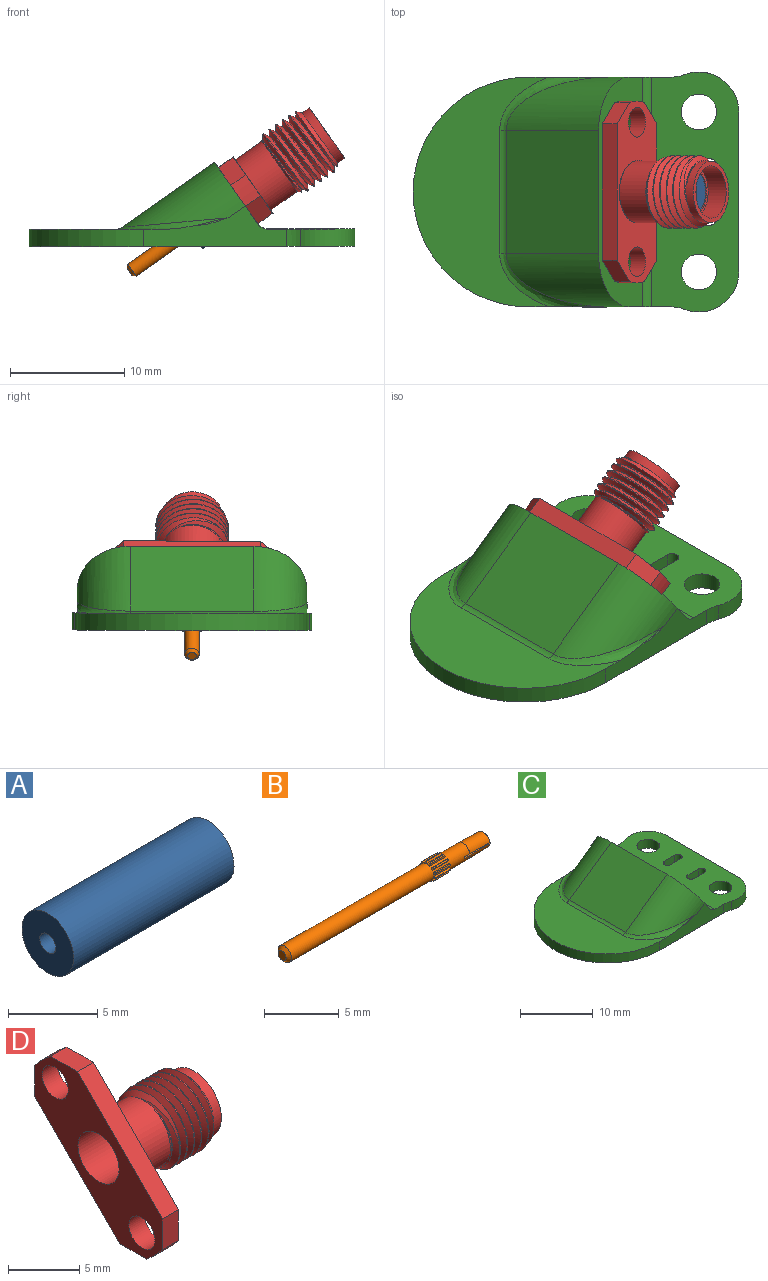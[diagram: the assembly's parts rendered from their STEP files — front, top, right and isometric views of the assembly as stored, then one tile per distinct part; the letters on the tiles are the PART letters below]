
ASSEMBLY  parts=4 mates=5
PART A: 4 faces, bbox 12.7x4.1x4.1 mm
  f0: plane 4.09x4.09mm, normal (-1,0,0), area 11.9mm2, adj f1,f3
  f1: cylinder r=0.64mm len=12.7mm, axis (-1,0,0), area 50.7mm2, adj f0,f2
  f2: plane 4.09x4.09mm, normal (1,0,0), area 11.9mm2, adj f1,f3
  f3: cylinder r=2.04mm len=12.7mm, axis (-1,0,0), area 163.2mm2, adj f0,f2
PART B: 81 faces, bbox 19.1x1.5x1.5 mm
  f0: cone r=0.76mm half-angle=60deg, axis (-1,0,0), area 0mm2, adj f1,f40,f76,f79
  f1: cylinder r=0.76mm len=1.38mm, axis (1,0,0), area 0.1mm2, adj f0,f2,f76,f79
  f2: cone r=0.64mm half-angle=60deg, axis (1,0,0), area 0mm2, adj f1,f40,f76,f79
  f3: cone r=0.76mm half-angle=60deg, axis (-1,0,0), area 0mm2, adj f4,f40,f74,f77
  f4: cylinder r=0.76mm len=1.38mm, axis (1,0,0), area 0.1mm2, adj f3,f5,f74,f77
  f5: cone r=0.64mm half-angle=60deg, axis (1,0,0), area 0mm2, adj f4,f40,f74,f77
  f6: cone r=0.76mm half-angle=60deg, axis (-1,0,0), area 0mm2, adj f7,f40,f72,f75
  f7: cylinder r=0.76mm len=1.38mm, axis (1,0,0), area 0.1mm2, adj f6,f8,f72,f75
  f8: cone r=0.64mm half-angle=60deg, axis (1,0,0), area 0mm2, adj f7,f40,f72,f75
  f9: cone r=0.76mm half-angle=60deg, axis (-1,0,0), area 0mm2, adj f10,f40,f70,f73
  f10: cylinder r=0.76mm len=1.38mm, axis (1,0,0), area 0.1mm2, adj f9,f11,f70,f73
  f11: cone r=0.64mm half-angle=60deg, axis (1,0,0), area 0mm2, adj f10,f40,f70,f73
  f12: cone r=0.76mm half-angle=60deg, axis (-1,0,0), area 0mm2, adj f13,f40,f68,f71
  f13: cylinder r=0.76mm len=1.38mm, axis (1,0,0), area 0.1mm2, adj f12,f14,f68,f71
  f14: cone r=0.64mm half-angle=60deg, axis (1,0,0), area 0mm2, adj f13,f40,f68,f71
  f15: cone r=0.76mm half-angle=60deg, axis (-1,0,0), area 0mm2, adj f16,f40,f66,f69
  f16: cylinder r=0.76mm len=1.38mm, axis (1,0,0), area 0.1mm2, adj f15,f17,f66,f69
  f17: cone r=0.64mm half-angle=60deg, axis (1,0,0), area 0mm2, adj f16,f40,f66,f69
  f18: cone r=0.76mm half-angle=60deg, axis (-1,0,0), area 0mm2, adj f19,f40,f64,f67
  f19: cylinder r=0.76mm len=1.38mm, axis (1,0,0), area 0.1mm2, adj f18,f20,f64,f67
  f20: cone r=0.64mm half-angle=60deg, axis (1,0,0), area 0mm2, adj f19,f40,f64,f67
  f21: cone r=0.76mm half-angle=60deg, axis (-1,0,0), area 0mm2, adj f22,f40,f63,f65
  f22: cylinder r=0.76mm len=1.38mm, axis (1,0,0), area 0.1mm2, adj f21,f23,f63,f65
  f23: cone r=0.64mm half-angle=60deg, axis (1,0,0), area 0mm2, adj f22,f40,f63,f65
  f24: cone r=0.76mm half-angle=60deg, axis (-1,0,0), area 0mm2, adj f25,f40,f60,f62
  f25: cylinder r=0.76mm len=1.38mm, axis (1,0,0), area 0.1mm2, adj f24,f26,f60,f62
  f26: cone r=0.64mm half-angle=60deg, axis (1,0,0), area 0mm2, adj f25,f40,f60,f62
  f27: cone r=0.76mm half-angle=60deg, axis (-1,0,0), area 0mm2, adj f28,f40,f58,f61
  f28: cylinder r=0.76mm len=1.38mm, axis (1,0,0), area 0.1mm2, adj f27,f29,f58,f61
  f29: cone r=0.64mm half-angle=60deg, axis (1,0,0), area 0mm2, adj f28,f40,f58,f61
  f30: cone r=0.76mm half-angle=60deg, axis (-1,0,0), area 0mm2, adj f31,f40,f56,f59
  f31: cylinder r=0.76mm len=1.38mm, axis (1,0,0), area 0.1mm2, adj f30,f32,f56,f59
  f32: cone r=0.64mm half-angle=60deg, axis (1,0,0), area 0mm2, adj f31,f40,f56,f59
  f33: plane 0.18x0.15mm, normal (1,0,0), area 0mm2, adj f36,f40,f42,f50
  f34: plane 0.18x0.15mm, normal (1,0,0), area 0mm2, adj f36,f40,f43,f49
  f35: cone r=0.46mm half-angle=59deg, axis (1,0,0), area 0.8mm2, adj f36
  f36: cylinder r=0.46mm len=1.02mm, axis (1,0,0), area 2.8mm2, adj f33,f34,f35,f42,f43,f47,f49,f50
  f37: cone r=0.76mm half-angle=60deg, axis (-1,0,0), area 0mm2, adj f38,f40,f57,f78
  f38: cylinder r=0.76mm len=1.38mm, axis (1,0,0), area 0.1mm2, adj f37,f39,f57,f78
  f39: cone r=0.64mm half-angle=60deg, axis (1,0,0), area 0mm2, adj f38,f40,f57,f78
  f40: cylinder r=0.64mm len=16.89mm, axis (1,0,0), area 64mm2, adj f0,f2,f3,f5,f6,f8,f9,f11
  f41: plane 0.76x0.76mm, normal (-1,0,0), area 0.5mm2, adj f80
  f42: plane 0.51x0.18mm, normal (0,0,-1), area 0.1mm2, adj f33,f36,f40,f46
  f43: plane 0.51x0.18mm, normal (0,0,-1), area 0.1mm2, adj f34,f36,f40,f48
  f44: plane 1.26x0.55mm, normal (1,0,0), area 0.3mm2, adj f45,f46,f47,f48
  f45: bspline ~1.91x1.26mm, area 3.5mm2, adj f40,f44,f46,f48
  f46: plane 1.91x0.18mm, normal (-0.03,0,-1), area 0.3mm2, adj f42,f44,f45,f47
  f47: bspline ~1.91x0.9mm, area 2.4mm2, adj f36,f44,f46,f48
  f48: plane 1.91x0.19mm, normal (-0.03,0,-1), area 0.3mm2, adj f43,f44,f45,f47
  f49: plane 0.51x0.18mm, normal (0,0,1), area 0.1mm2, adj f34,f36,f40,f52
  f50: plane 0.51x0.18mm, normal (0,0,1), area 0.1mm2, adj f33,f36,f40,f54
  f51: plane 1.26x0.55mm, normal (1,0,0), area 0.3mm2, adj f52,f53,f54,f55
  f52: plane 1.91x0.19mm, normal (-0.03,0,1), area 0.3mm2, adj f49,f51,f53,f55
  f53: bspline ~1.91x0.9mm, area 2.4mm2, adj f36,f51,f52,f54
  f54: plane 1.91x0.18mm, normal (-0.03,0,1), area 0.3mm2, adj f50,f51,f53,f55
  f55: bspline ~1.91x1.26mm, area 3.5mm2, adj f40,f51,f52,f54
  f56: plane 1.53x0.12mm, normal (0,-0.87,0.5), area 0.2mm2, adj f30,f31,f32,f40
  f57: plane 1.53x0.12mm, normal (0,0.87,0.5), area 0.2mm2, adj f37,f38,f39,f40
  f58: plane 1.53x0.12mm, normal (0,-0.5,0.87), area 0.2mm2, adj f27,f28,f29,f40
  f59: plane 1.53x0.14mm, normal (0,1,0), area 0.2mm2, adj f30,f31,f32,f40
  f60: plane 1.53x0.14mm, normal (0,0,1), area 0.2mm2, adj f24,f25,f26,f40
  f61: plane 1.53x0.12mm, normal (0,0.87,-0.5), area 0.2mm2, adj f27,f28,f29,f40
  f62: plane 1.53x0.12mm, normal (0,0.5,-0.87), area 0.2mm2, adj f24,f25,f26,f40
  f63: plane 1.53x0.12mm, normal (0,0.5,0.87), area 0.2mm2, adj f21,f22,f23,f40
  f64: plane 1.53x0.12mm, normal (0,0.87,0.5), area 0.2mm2, adj f18,f19,f20,f40
  f65: plane 1.53x0.14mm, normal (0,0,-1), area 0.2mm2, adj f21,f22,f23,f40
  f66: plane 1.53x0.14mm, normal (0,1,0), area 0.2mm2, adj f15,f16,f17,f40
  f67: plane 1.53x0.12mm, normal (0,-0.5,-0.87), area 0.2mm2, adj f18,f19,f20,f40
  f68: plane 1.53x0.12mm, normal (0,0.87,-0.5), area 0.2mm2, adj f12,f13,f14,f40
  f69: plane 1.53x0.12mm, normal (0,-0.87,-0.5), area 0.2mm2, adj f15,f16,f17,f40
  f70: plane 1.53x0.12mm, normal (0,0.5,-0.87), area 0.2mm2, adj f9,f10,f11,f40
  f71: plane 1.53x0.14mm, normal (0,-1,0), area 0.2mm2, adj f12,f13,f14,f40
  f72: plane 1.53x0.14mm, normal (0,0,-1), area 0.2mm2, adj f6,f7,f8,f40
  f73: plane 1.53x0.12mm, normal (0,-0.87,0.5), area 0.2mm2, adj f9,f10,f11,f40
  f74: plane 1.53x0.12mm, normal (0,-0.5,-0.87), area 0.2mm2, adj f3,f4,f5,f40
  f75: plane 1.53x0.12mm, normal (0,-0.5,0.87), area 0.2mm2, adj f6,f7,f8,f40
  f76: plane 1.53x0.12mm, normal (0,-0.87,-0.5), area 0.2mm2, adj f0,f1,f2,f40
  f77: plane 1.53x0.14mm, normal (0,0,1), area 0.2mm2, adj f3,f4,f5,f40
  f78: plane 1.53x0.14mm, normal (0,-1,0), area 0.2mm2, adj f37,f38,f39,f40
  f79: plane 1.53x0.12mm, normal (0,0.5,0.87), area 0.2mm2, adj f0,f1,f2,f40
  f80: cone r=0.64mm half-angle=45deg, axis (1,0,0), area 1.1mm2, adj f40,f41
PART C: 32 faces, bbox 28.9x22.5x11.9 mm
  f0: plane 21x7.65mm, normal (0,0,1), area 130.7mm2, adj f2,f3,f4,f5,f6,f7,f9,f10
  f1: plane 20.1x11.83mm, normal (0,0,1), area 120.9mm2, adj f7,f8,f19,f29,f30,f31
  f2: cylinder r=3.5mm len=1.5mm, axis (0,0,1), area 1.9mm2, adj f0,f3,f19,f20
  f3: cylinder r=3.5mm len=4.74mm, axis (0,0,1), area 10.1mm2, adj f0,f2,f4,f20
  f4: plane 14x1.53mm, normal (1,0,0), area 21mm2, adj f0,f3,f5,f20
  f5: cylinder r=3.5mm len=4.74mm, axis (0,0,1), area 10.1mm2, adj f0,f4,f6,f20
  f6: cylinder r=3.5mm len=1.5mm, axis (0,0,1), area 1.9mm2, adj f0,f5,f7,f20
  f7: plane 12.92x3.98mm, normal (0,1,0), area 24.7mm2, adj f0,f1,f6,f8,f20,f25,f27,f28
  f8: cylinder r=10.05mm len=20.1mm, axis (0,0,1), area 47.4mm2, adj f1,f7,f19,f20
  f9: plane 2x1.5mm, normal (0,1,0), area 3mm2, adj f0,f10,f17,f20
  f10: cylinder r=0.6mm len=1.5mm, axis (0,0,1), area 2.8mm2, adj f0,f9,f11,f20
  f11: plane 2x1.5mm, normal (0,-1,0), area 3mm2, adj f0,f10,f17,f20
  f12: plane 2x1.5mm, normal (0,1,0), area 3mm2, adj f0,f13,f18,f20
  f13: cylinder r=0.6mm len=1.5mm, axis (0,0,1), area 2.8mm2, adj f0,f12,f14,f20
  f14: plane 2x1.5mm, normal (0,-1,0), area 3mm2, adj f0,f13,f18,f20
  f15: cylinder r=1.55mm len=3.1mm, axis (0,0,1), area 14.6mm2, adj f0,f20
  f16: cylinder r=1.55mm len=3.1mm, axis (0,0,1), area 14.6mm2, adj f0,f20
  f17: cylinder r=0.6mm len=1.5mm, axis (0,0,1), area 2.8mm2, adj f0,f9,f11,f20
  f18: cylinder r=0.6mm len=1.5mm, axis (0,0,1), area 2.8mm2, adj f0,f12,f14,f20
  f19: plane 12.92x3.98mm, normal (0,-1,0), area 24.7mm2, adj f0,f1,f2,f8,f20,f21,f27,f28
  f20: plane 28.78x21.26mm, normal (0,0,-1), area 454mm2, adj f2,f3,f4,f5,f6,f7,f8,f9
  f21: cylinder r=4.64mm len=10.75mm, axis (0.82,0,0.58), area 50.7mm2, adj f19,f22,f27,f31
  f22: plane 10.83x8.08mm, normal (-0.58,0,0.82), area 106.9mm2, adj f21,f25,f27,f30
  f23: cylinder r=1.3mm len=9.33mm, axis (0.82,0,0.58), area 63.1mm2, adj f20,f27
  f24: cylinder r=2.5mm len=12.14mm, axis (0.82,0,0.58), area 121.1mm2, adj f20,f27
  f25: cylinder r=4.64mm len=10.75mm, axis (0.82,0,0.58), area 50.7mm2, adj f7,f22,f27,f29
  f26: cylinder r=1.3mm len=9.33mm, axis (0.82,0,0.58), area 63.1mm2, adj f20,f27
  f27: plane 20.1x5.44mm, normal (0.82,0,0.58), area 93.5mm2, adj f7,f19,f21,f22,f23,f24,f25,f26
  f28: cylinder r=1mm len=20.1mm, axis (0,-1,0), area 19.3mm2, adj f0,f7,f19,f27
  f29: bspline ~10.26x6.62mm, area 8.4mm2, adj f1,f7,f25,f30
  f30: cylinder r=1mm len=10.82mm, axis (0,-1,0), area 6.6mm2, adj f1,f22,f29,f31
  f31: bspline ~9.83x5.64mm, area 8.4mm2, adj f1,f19,f21,f30
PART D: 34 faces, bbox 9.7x12.9x12.9 mm
  f0: plane 12.7x12.7mm, normal (-1,0,0), area 63.7mm2, adj f2,f3,f4,f5,f19,f20,f25,f26
  f1: plane 12.86x12.86mm, normal (1,0,0), area 52mm2, adj f2,f3,f4,f5,f7,f9,f19,f20
  f2: plane 2.66x1.6mm, normal (0,-1,0), area 4.2mm2, adj f0,f1,f20,f31
  f3: plane 2.66x1.6mm, normal (0,0,-1), area 4.2mm2, adj f0,f1,f20,f32
  f4: plane 2.66x1.6mm, normal (0,1,0), area 4.2mm2, adj f0,f1,f19,f32
  f5: plane 2.66x1.6mm, normal (0,0,1), area 4.2mm2, adj f0,f1,f19,f31
  f6: cylinder r=3.17mm len=6.35mm, axis (1,0,0), area 71.9mm2, adj f8,f10,f29,f30
  f7: cylinder r=3.17mm len=1.08mm, axis (1,0,0), area 0mm2, adj f1,f9,f23,f28
  f8: bspline ~7.21x7.21mm, area 35.3mm2, adj f6,f12,f13,f14,f15,f16,f17,f18
  f9: bspline ~6.35x3.67mm, area 0.2mm2, adj f1,f7,f23,f24,f33
  f10: bspline ~6.34x6.09mm, area -4.5mm2, adj f6,f12,f13,f14,f15,f16,f17,f18
  f11: plane 5.38x5.38mm, normal (1,0,0), area 6.2mm2, adj f13,f22
  f12: cylinder r=2.69mm len=5.39mm, axis (1,0,0), area 48.5mm2, adj f8,f10,f18,f23,f30
  f13: cylinder r=2.69mm len=5.39mm, axis (1,0,0), area 13.7mm2, adj f8,f10,f11,f14,f29
  f14: cylinder r=2.69mm len=5.38mm, axis (1,0,0), area -1.1mm2, adj f8,f10,f13,f15
  f15: cylinder r=2.69mm len=5.38mm, axis (1,0,0), area 1.2mm2, adj f8,f10,f14,f16
  f16: cylinder r=2.69mm len=5.38mm, axis (1,0,0), area -1.4mm2, adj f8,f10,f15,f17
  f17: cylinder r=2.69mm len=5.39mm, axis (1,0,0), area 1.2mm2, adj f8,f10,f16,f18
  f18: cylinder r=2.69mm len=5.38mm, axis (1,0,0), area 0.2mm2, adj f8,f10,f12,f17
  f19: cylinder r=7.94mm len=1.6mm, axis (1,0,0), area 3.6mm2, adj f0,f1,f4,f5
  f20: cylinder r=7.94mm len=1.6mm, axis (1,0,0), area 3.6mm2, adj f0,f1,f2,f3
  f21: plane 4.6x4.6mm, normal (1,0,0), area 3.5mm2, adj f22,f25
  f22: cylinder r=2.3mm len=4.6mm, axis (1,0,0), area 27.9mm2, adj f11,f21
  f23: plane 5.88x5.65mm, normal (1,0,0), area 2.3mm2, adj f7,f9,f12,f24,f28
  f24: cylinder r=2.7mm len=5.41mm, axis (1,0,0), area 0.1mm2, adj f1,f9,f23,f28
  f25: cylinder r=2.04mm len=7.59mm, axis (1,0,0), area 97.6mm2, adj f0,f21
  f26: cylinder r=1.3mm len=2.6mm, axis (1,0,0), area 13.1mm2, adj f0,f1
  f27: cylinder r=1.3mm len=2.6mm, axis (1,0,0), area 13.1mm2, adj f0,f1
  f28: plane 0.47x0.01mm, normal (0,-1,0), area 0mm2, adj f1,f7,f23,f24
  f29: cone r=3.33mm half-angle=45deg, axis (-1,0,0), area 6.2mm2, adj f6,f8,f10,f13
  f30: cone r=2.69mm half-angle=45deg, axis (1,0,0), area 6.2mm2, adj f6,f8,f10,f12
  f31: plane 8.46x8.46mm, normal (0,-0.71,0.71), area 19.1mm2, adj f0,f1,f2,f5
  f32: plane 8.46x8.46mm, normal (0,0.71,-0.71), area 19.1mm2, adj f0,f1,f3,f4,f33
  f33: plane 0.99x0.99mm, normal (-1,0,0), area 0.1mm2, adj f9,f32
PLACE A rot(axis=(0.27,-0.96,0.08),36.5deg) t=(-6.23,-2.54,0.37)mm
PLACE B rot(axis=(-0.77,-0.59,-0.24),56.4deg) t=(4.12,-2.55,7.65)mm
PLACE C at identity fixed
PLACE D rot(axis=(-0.77,-0.59,-0.24),56.4deg) t=(4.24,-2.55,7.74)mm
MATE slider B.f0 <-> D.f29  axis (0.82,0,0.58) through (-4.35,-2.54,1.7)mm
MATE fastened C.f26 <-> D.f27  axis (0.82,0,0.58) through (-1.97,-8.65,3.36)mm
MATE cylindrical A.f1 <-> D.f12  axis (-0.82,0,-0.58) through (-1.03,-2.54,4.03)mm
MATE planar B.f51 <-> A.f1  axis (0.82,0,0.58) through (4.25,-2.78,7.47)mm
MATE planar A.f1 <-> D.f6  axis (0.82,0,0.58) through (4.16,-2.55,7.68)mm
